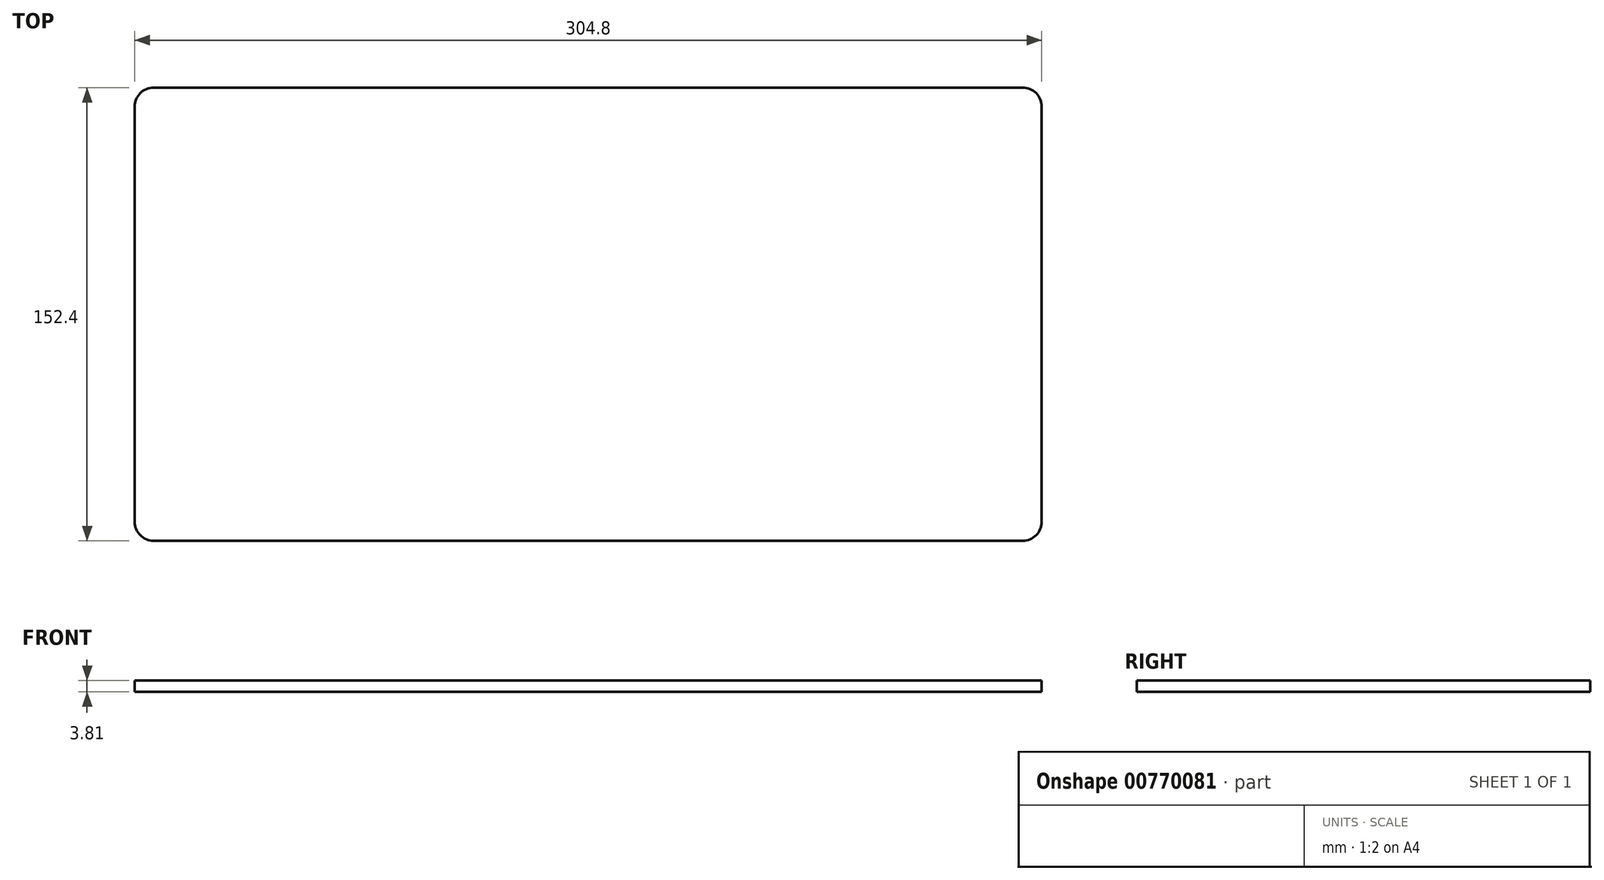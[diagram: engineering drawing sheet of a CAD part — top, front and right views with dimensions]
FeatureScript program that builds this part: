
annotation { "Feature Type Name" : "Feature", "Feature Type Description" : "" }
export const myFeature = defineFeature(function(context is Context, id is Id, definition is map)
    precondition{}
    {
        {
            var Q0;
            Q0=qCreatedBy(makeId("Top.planeOp"),FACE);
            var sketch = newSketch(context, id + "F0", { "sketchPlane" : qUnion([Q0])});
            skLineSegment(sketch, "E0.bottom", {"start": v(146.05, 76.2) * mm, "end": v(-146.05, 76.2) * mm});
            skLineSegment(sketch, "E0.top", {"start": v(146.05, -76.2) * mm, "end": v(-146.05, -76.2) * mm});
            skLineSegment(sketch, "E0.left", {"start": v(152.4, 69.85) * mm, "end": v(152.4, -69.85) * mm});
            skLineSegment(sketch, "E0.right", {"start": v(-152.4, 69.85) * mm, "end": v(-152.4, -69.85) * mm});
            skPoint(sketch, "E0.middle", {"position": v(0, 0) * mm});
            skPoint(sketch, "E1.visualSharp", {"position": v(-152.4, 76.2) * mm});
            skArc(sketch, "E1.filletArc", {"start": v(-146.05, 76.2) * mm, "mid": v(-150.54, 74.34) * mm, "end": v(-152.4, 69.85) * mm});
            skPoint(sketch, "E2.visualSharp", {"position": v(152.4, 76.2) * mm});
            skArc(sketch, "E2.filletArc", {"start": v(152.4, 69.85) * mm, "mid": v(150.54, 74.34) * mm, "end": v(146.05, 76.2) * mm});
            skPoint(sketch, "E3.visualSharp", {"position": v(152.4, -76.2) * mm});
            skArc(sketch, "E3.filletArc", {"start": v(146.05, -76.2) * mm, "mid": v(150.54, -74.34) * mm, "end": v(152.4, -69.85) * mm});
            skPoint(sketch, "E4.visualSharp", {"position": v(-152.4, -76.2) * mm});
            skArc(sketch, "E4.filletArc", {"start": v(-152.4, -69.85) * mm, "mid": v(-150.54, -74.34) * mm, "end": v(-146.05, -76.2) * mm});
            skSolve(sketch);
        }
        {
            var Q0;
            Q0=makeQuery(id+"F0.imprint","IMPRINT",FACE,{"disambiguationData":[TD([[makeQuery(id+"F0.imprint","IMPRINT",EDGE,{"derivedFrom":sQuery(id+"F0.wireOp",EDGE,"E0.bottom")}),1.0]])]});
            extrude(context, id + "F1", {"entities" : qUnion([Q0]), "depth" : 3.8 * mm, "offsetDistance" : 25.4 * mm});
        }
    });
